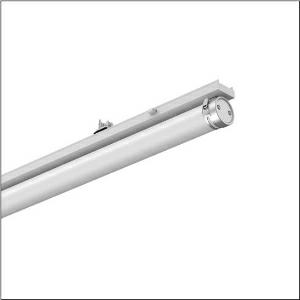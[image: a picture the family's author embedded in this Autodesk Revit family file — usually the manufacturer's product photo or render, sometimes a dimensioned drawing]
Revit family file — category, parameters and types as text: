
# Revit family: monsun_r__31_tube_51ft10mn4a0atr1_8ef5
name_source: partatom
category: Lighting Fixtures
units: mm (PartAtom-declared; Revit-internal decimal feet)

## family parameters
Cut with Voids When Loaded = No
Host = Face
Light Source = No
Part Type = Normal
Room Calculation Point = No
Round Connector Dimension = Use Diameter
Shared = No

## types (1)
- --- (1 x LED, 10000 lm, 58 W, 4000K)
    Apparent Load = 58 VA
    CIE Flux Codes = 42 71 90 91 100
    Color Rendering = 80
    Color Temperature = 4000K
    Default Elevation = 1800 mm
    Description = Monsun® 31 Tube, tubular luminaire, primary optical cover: diffuser, of PMMA, light emission: direct distribution, primary light characteristic: symmetric, LED, rated luminous flux: 10.000lm, luminous efficacy: 172lm/W, light colour: 840, colour temperature: 4000K, control gear: ON/OFF Multilumen, with with 1 terminal, 3-pole, max. 2.5mm², mains connection: 220..240V, AC, 50/60Hz, rated input power: 58W, housing, cylindrical, of PMMA, semi-transparent, matt white, with luminaire and ceiling fastening, V4A, mounting with brackets of stainless steel, length: 1.495mm, diameter: 75mm, end cap, of stainless steel (V4A), protection rating (complete): IP20, protection rating (lamp compartment): IP67/69K, insulation class (complete): insulation class I (protective earthing), certification: CE, UKCA, impact resistance: IK07, permissible operating ambient temperature: -20..+40°C, corresponds to IFS (International Featured Standards) requirements for safety and quality in the food industry, contact your sales advisor before using the luminaires in applications with unclear chemical exposure, large temperature fluctuations or condensation-forming humidity, packaging unit: 1 piece
    Height = 118 mm
    Lamp = 1 x LED
    Lamp Light Flux = 10000 lm
    Lamp Power = 58 W
    Lamp count = 1
    Length = 1495 mm
    Luminous efficacy = 172 lm/W
    Manufacturer = Siteco
    ModVariant = No
    Model = 51FT10MN4A0ATR1
    Mounting Place = Ceiling
    Mounting Type = Pendant
    Number of Poles = 1
    OnlyDefault = Yes
    Power Factor = 1
    Product Name = Monsun® 31 Tube
    Product group = tubular luminaire
    ProductGroupID = 907
    Protection Class = Protection class I
    Protection Degree = IP 20
    RLX_Detail_Level = 1
    RLX_Emergency_Light_Flux = 0 lm
    RLX_Emergency_Type = 0
    RLX_Emergency_Type_DB = No
    RlxData = <blob elided: 32353 chars, md5=f3a0f410>
    Socket = socket
    Standby Power = 0 W
    System Light Flux = 10000 lm
    System Power = 58 W
    Type Comments = factory setting: luminous flux: 100 % | (OFF | OFF | OFF | OFF) | 350 mA
    Type Image = l_1007227.jpg
    URL = http://relux.com
    VarID = @adj_143378
    Voltage = 0 V
    Weight = 0.00 kg
    Width = 75 mm

## geometry (parser evidence)
native form markers: Blend x4, Sweep x12
no freeform markers — native parametric forms only
